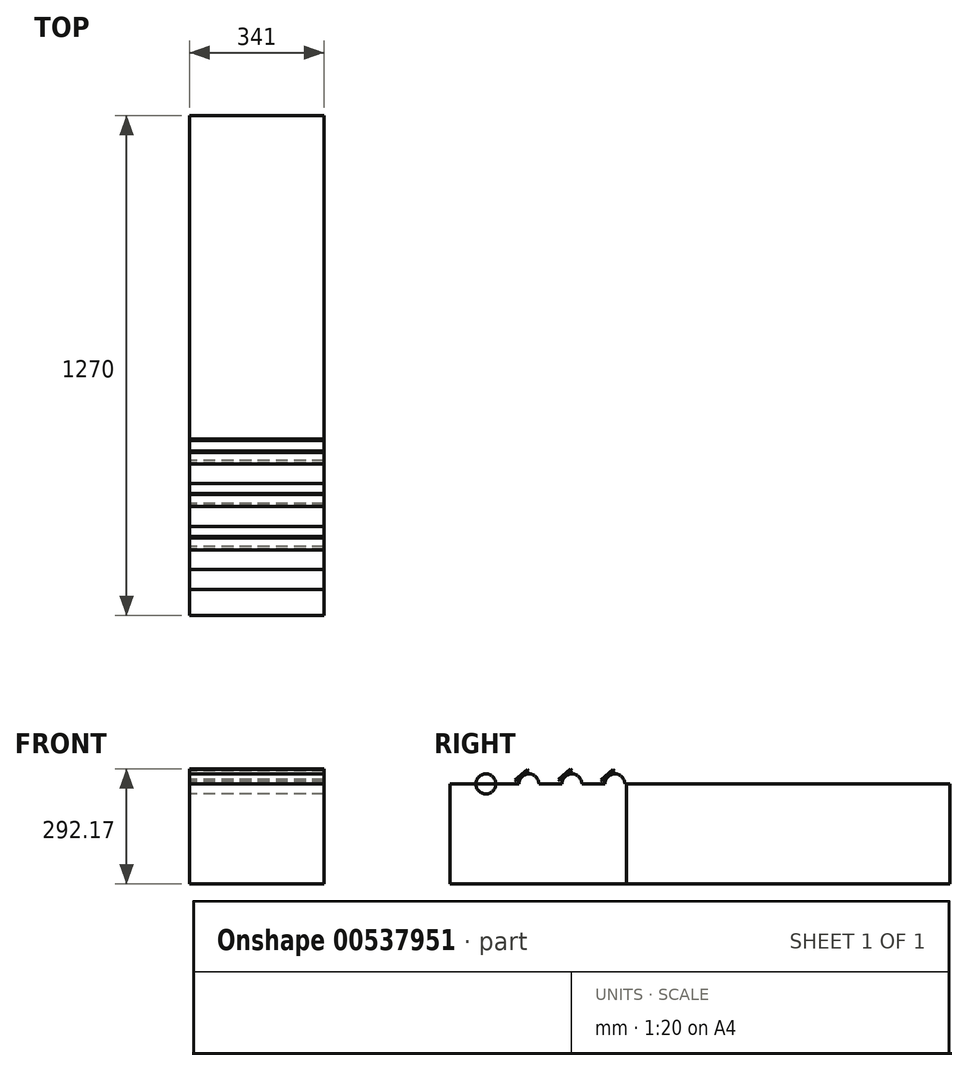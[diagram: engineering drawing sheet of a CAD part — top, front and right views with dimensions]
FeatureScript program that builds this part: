
annotation { "Feature Type Name" : "Feature", "Feature Type Description" : "" }
export const myFeature = defineFeature(function(context is Context, id is Id, definition is map)
    precondition{}
    {
        {
            var Q0;
            Q0=qCreatedBy(makeId("Top.planeOp"),FACE);
            var sketch = newSketch(context, id + "F0", { "sketchPlane" : qUnion([Q0])});
            skLineSegment(sketch, "E0.bottom", {"start": v(170.5, 635) * mm, "end": v(-170.5, 635) * mm});
            skLineSegment(sketch, "E0.top", {"start": v(170.5, -635) * mm, "end": v(-170.5, -635) * mm});
            skLineSegment(sketch, "E0.left", {"start": v(170.5, 635) * mm, "end": v(170.5, -635) * mm});
            skLineSegment(sketch, "E0.right", {"start": v(-170.5, 635) * mm, "end": v(-170.5, -635) * mm});
            skPoint(sketch, "E0.middle", {"position": v(0, 0) * mm});
            skLineSegment(sketch, "E1", {"start": v(-170.5, -568.96) * mm, "end": v(170.5, -568.96) * mm});
            skLineSegment(sketch, "E2", {"start": v(-170.5, -518.16) * mm, "end": v(170.5, -518.16) * mm});
            skLineSegment(sketch, "E3", {"start": v(-170.5, -543.56) * mm, "end": v(170.5, -543.56) * mm});
            skLineSegment(sketch, "E4", {"start": v(-170.5, -434.34) * mm, "end": v(170.5, -434.34) * mm});
            skLineSegment(sketch, "E5", {"start": v(-170.5, -459.74) * mm, "end": v(170.5, -459.74) * mm});
            skLineSegment(sketch, "E6", {"start": v(-170.5, -408.94) * mm, "end": v(170.5, -408.94) * mm});
            skLineSegment(sketch, "E7.MirrorCS", {"start": v(-170.5, -350.52) * mm, "end": v(170.5, -350.52) * mm});
            skLineSegment(sketch, "E8.MirrorCS", {"start": v(-170.5, -325.12) * mm, "end": v(170.5, -325.12) * mm});
            skLineSegment(sketch, "E9.MirrorCS", {"start": v(-170.5, -297.9) * mm, "end": v(170.5, -297.9) * mm});
            skLineSegment(sketch, "E10.MirrorCS", {"start": v(-170.5, -186.87) * mm, "end": v(170.5, -186.87) * mm});
            skLineSegment(sketch, "E11.MirrorCS", {"start": v(-170.5, -212.27) * mm, "end": v(170.5, -212.27) * mm});
            skLineSegment(sketch, "E12.MirrorCS", {"start": v(-170.5, -239.49) * mm, "end": v(170.5, -239.49) * mm});
            skSolve(sketch);
        }
        {
            var Q0;
            Q0=qCreatedBy(makeId("Right.planeOp"),FACE);
            var sketch = newSketch(context, id + "F1", { "sketchPlane" : qUnion([Q0])});
            skCircle(sketch, "E13", {"center": v(-543.56, 0) * mm, "radius": 25.4 * mm});
            skCircle(sketch, "E14", {"center": v(-434.34, 0) * mm, "radius": 25.4 * mm});
            skCircle(sketch, "E15", {"center": v(-325.12, 0) * mm, "radius": 25.4 * mm});
            skCircle(sketch, "E16", {"center": v(-215.9, 0) * mm, "radius": 25.4 * mm});
            skSolve(sketch);
        }
        {
            var Q0;
            Q0=makeQuery(id+"F1.imprint","IMPRINT",FACE,{"disambiguationData":[TD([[makeQuery(id+"F1.imprint","IMPRINT",EDGE,{"derivedFrom":sQuery(id+"F1.wireOp",EDGE,"E13")}),1.0]])]});
            extrude(context, id + "F2", {"entities" : qUnion([Q0]), "depth" : 170.5 * mm, "offsetDistance" : 25.4 * mm});
        }
        {
            var Q0;
            Q0=makeQuery(id+"F2.opExtrude","CAP_FACE",FACE,{"disambiguationData":[OSD([sQuery(id+"F1.wireOp",EDGE,"E13")])],"isStart":false});
            extrude(context, id + "F3", {"entities" : qUnion([Q0]), "operationType" : NewBodyOperationType.ADD, "oppositeDirection" : true, "depth" : 341 * mm, "offsetDistance" : 25.4 * mm});
        }
        {
            var Q0;
            {var subQ0=sQuery(id+"F0.wireOp",EDGE,"E0.bottom");Q0=makeQuery(id+"F0.imprint","IMPRINT",FACE,{"disambiguationData":[TD([[makeQuery(id+"F0.imprint","IMPRINT",EDGE,{"derivedFrom":subQ0}),1.0]])]});}
            extrude(context, id + "F4", {"entities" : qUnion([Q0]), "oppositeDirection" : true, "depth" : 254 * mm, "offsetDistance" : 25.4 * mm});
        }
        {
            var Q0;
            Q0 = qSketchRegion(id + "F0", true);
            var Q1;
            Q1=makeQuery(id+"F4.opExtrude","CAP_FACE",FACE,{"disambiguationData":[OSD([sQuery(id+"F0.wireOp",EDGE,"E0.bottom"),sQuery(id+"F0.wireOp",EDGE,"E0.left"),sQuery(id+"F0.wireOp",EDGE,"E0.right"),sQuery(id+"F0.wireOp",EDGE,"E2")])],"isStart":true});
            extrude(context, id + "F5", {"entities" : qUnion([Q0, Q1]), "oppositeDirection" : true, "depth" : 254 * mm, "offsetDistance" : 25.4 * mm});
        }
        {
            var Q0;
            Q0=makeQuery(id+"F1.imprint","IMPRINT",FACE,{"disambiguationData":[TD([[makeQuery(id+"F1.imprint","IMPRINT",EDGE,{"derivedFrom":sQuery(id+"F1.wireOp",EDGE,"E14")}),1.0]])]});
            extrude(context, id + "F6", {"entities" : qUnion([Q0]), "operationType" : NewBodyOperationType.ADD, "endBound" : BoundingType.SYMMETRIC, "depth" : 341 * mm, "offsetDistance" : 25.4 * mm});
        }
        {
            var Q0;
            Q0=qCreatedBy(makeId("Right.planeOp"),FACE);
            var sketch = newSketch(context, id + "F7", { "sketchPlane" : qUnion([Q0])});
            skLineSegment(sketch, "E17", {"start": v(-465.9, 6.68) * mm, "end": v(-434.76, 32.8) * mm});
            skLineSegment(sketch, "E18", {"start": v(-465.9, 6.68) * mm, "end": v(-469.17, 10.57) * mm});
            skLineSegment(sketch, "E19", {"start": v(-438.03, 36.69) * mm, "end": v(-469.17, 10.57) * mm});
            skLineSegment(sketch, "E20", {"start": v(-438.03, 36.69) * mm, "end": v(-434.76, 32.8) * mm});
            skLineSegment(sketch, "E21", {"start": v(-355.06, 7.32) * mm, "end": v(-324.74, 34.38) * mm});
            skLineSegment(sketch, "E22", {"start": v(-324.74, 34.38) * mm, "end": v(-328.12, 38.17) * mm});
            skLineSegment(sketch, "E23", {"start": v(-328.12, 38.17) * mm, "end": v(-358.44, 11.11) * mm});
            skLineSegment(sketch, "E24", {"start": v(-358.44, 11.11) * mm, "end": v(-355.06, 7.32) * mm});
            skLineSegment(sketch, "E25", {"start": v(-247.45, 5.88) * mm, "end": v(-217.13, 32.95) * mm});
            skLineSegment(sketch, "E26", {"start": v(-217.13, 32.95) * mm, "end": v(-220.51, 36.74) * mm});
            skLineSegment(sketch, "E27", {"start": v(-220.51, 36.74) * mm, "end": v(-250.83, 9.67) * mm});
            skLineSegment(sketch, "E28", {"start": v(-250.83, 9.67) * mm, "end": v(-247.45, 5.88) * mm});
            skSolve(sketch);
        }
        {
            var Q0;
            Q0=makeQuery(id+"F7.imprint","IMPRINT",FACE,{"disambiguationData":[TD([[makeQuery(id+"F7.imprint","IMPRINT",EDGE,{"derivedFrom":sQuery(id+"F7.wireOp",EDGE,"E17")}),1.0]])]});
            extrude(context, id + "F8", {"entities" : qUnion([Q0]), "operationType" : NewBodyOperationType.ADD, "endBound" : BoundingType.SYMMETRIC, "depth" : 341 * mm, "offsetDistance" : 25.4 * mm});
        }
        {
            var Q0;
            Q0=makeQuery(id+"F1.imprint","IMPRINT",FACE,{"disambiguationData":[TD([[makeQuery(id+"F1.imprint","IMPRINT",EDGE,{"derivedFrom":sQuery(id+"F1.wireOp",EDGE,"E15")}),1.0]])]});
            extrude(context, id + "F9", {"entities" : qUnion([Q0]), "operationType" : NewBodyOperationType.ADD, "endBound" : BoundingType.SYMMETRIC, "depth" : 341 * mm, "offsetDistance" : 25.4 * mm});
        }
        {
            var Q0;
            Q0=makeQuery(id+"F1.imprint","IMPRINT",FACE,{"disambiguationData":[TD([[makeQuery(id+"F1.imprint","IMPRINT",EDGE,{"derivedFrom":sQuery(id+"F1.wireOp",EDGE,"E16")}),1.0]])]});
            extrude(context, id + "F10", {"entities" : qUnion([Q0]), "operationType" : NewBodyOperationType.ADD, "endBound" : BoundingType.SYMMETRIC, "depth" : 341 * mm, "offsetDistance" : 25.4 * mm});
        }
        {
            var Q0;
            Q0=makeQuery(id+"F7.imprint","IMPRINT",FACE,{"disambiguationData":[TD([[makeQuery(id+"F7.imprint","IMPRINT",EDGE,{"derivedFrom":sQuery(id+"F7.wireOp",EDGE,"E21")}),1.0]])]});
            extrude(context, id + "F11", {"entities" : qUnion([Q0]), "operationType" : NewBodyOperationType.ADD, "endBound" : BoundingType.SYMMETRIC, "depth" : 341 * mm, "offsetDistance" : 25.4 * mm});
        }
        {
            var Q0;
            Q0=makeQuery(id+"F7.imprint","IMPRINT",FACE,{"disambiguationData":[TD([[makeQuery(id+"F7.imprint","IMPRINT",EDGE,{"derivedFrom":sQuery(id+"F7.wireOp",EDGE,"E25")}),1.0]])]});
            extrude(context, id + "F12", {"entities" : qUnion([Q0]), "operationType" : NewBodyOperationType.ADD, "endBound" : BoundingType.SYMMETRIC, "depth" : 341 * mm, "offsetDistance" : 25.4 * mm});
        }
    });
